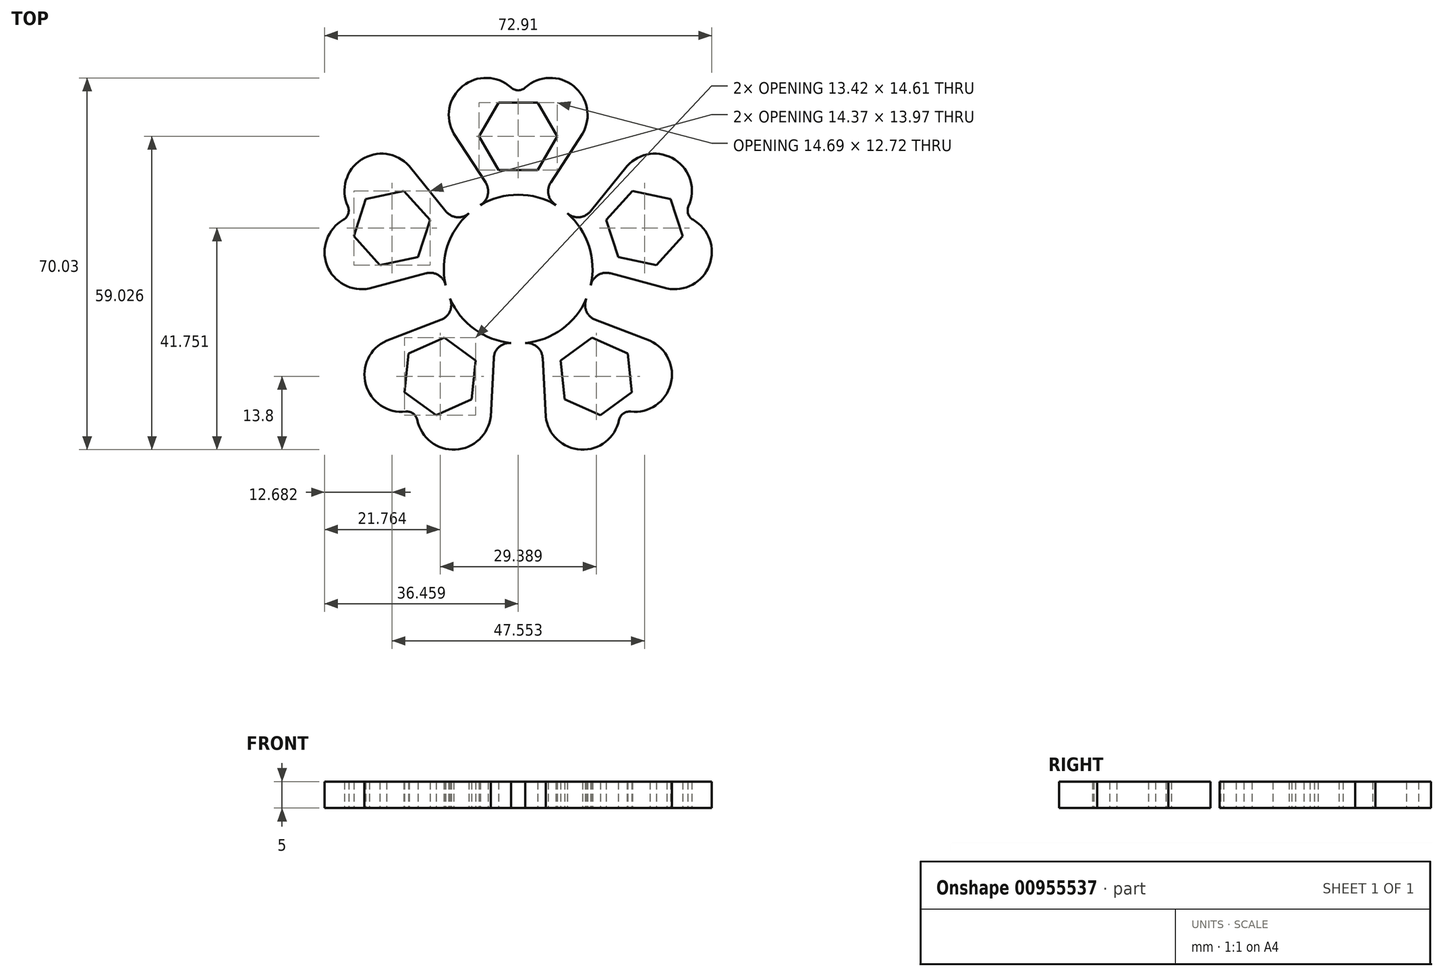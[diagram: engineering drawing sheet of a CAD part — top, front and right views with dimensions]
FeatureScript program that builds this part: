
annotation { "Feature Type Name" : "Feature", "Feature Type Description" : "" }
export const myFeature = defineFeature(function(context is Context, id is Id, definition is map)
    precondition{}
    {
        {
            var Q0;
            Q0=qCreatedBy(makeId("Top.planeOp"),FACE);
            var sketch = newSketch(context, id + "F0", { "sketchPlane" : qUnion([Q0])});
            skLineSegment(sketch, "E0", {"start": v(6.13, 16.29) * mm, "end": v(12.12, 25.52) * mm});
            skArc(sketch, "E1", {"start": v(12.12, 25.52) * mm, "mid": v(10.45, 34.47) * mm, "end": v(1.35, 34.19) * mm});
            skLineSegment(sketch, "E2.trimOffspring", {"start": v(0, 32.52) * mm, "end": v(0, 67.12) * mm, "construction": true});
            skLineSegment(sketch, "E3.trimOffspring", {"start": v(0, 19.02) * mm, "end": v(0, 41.02) * mm, "construction": true});
            skArc(sketch, "E4.MirrorCS", {"start": v(-12.13, 25.52) * mm, "mid": v(-10.45, 34.47) * mm, "end": v(-1.35, 34.19) * mm});
            skPoint(sketch, "E5.visualSharp", {"position": v(0, 32.52) * mm});
            skArc(sketch, "E5.filletArc", {"start": v(-1.35, 34.19) * mm, "mid": v(0, 33.67) * mm, "end": v(1.35, 34.19) * mm});
            skCircle(sketch, "E6.cCircle", {"center": v(0, 25.02) * mm, "radius": 6.36 * mm, "construction": true});
            skLineSegment(sketch, "E6.0", {"start": v(-3.67, 31.38) * mm, "end": v(3.67, 31.38) * mm});
            skLineSegment(sketch, "E6.1", {"start": v(3.67, 31.38) * mm, "end": v(7.34, 25.02) * mm});
            skLineSegment(sketch, "E6.2", {"start": v(7.34, 25.02) * mm, "end": v(3.67, 18.66) * mm});
            skLineSegment(sketch, "E6.3", {"start": v(3.67, 18.66) * mm, "end": v(-3.67, 18.66) * mm});
            skLineSegment(sketch, "E6.4", {"start": v(-3.67, 18.66) * mm, "end": v(-7.35, 25.02) * mm});
            skLineSegment(sketch, "E6.5", {"start": v(-7.35, 25.02) * mm, "end": v(-3.67, 31.38) * mm});
            skPoint(sketch, "E6.0.midPoint", {"position": v(0, 31.38) * mm});
            skCircle(sketch, "E7.0", {"center": v(0, 0.02) * mm, "radius": 14 * mm});
            skArc(sketch, "E8", {"start": v(6.13, 16.29) * mm, "mid": v(5.72, 13.97) * mm, "end": v(7.12, 12.07) * mm});
            skPoint(sketch, "E9.orphan", {"position": v(1.19, 8.67) * mm});
            skPoint(sketch, "E10.orphan", {"position": v(-1.19, 8.67) * mm});
            skArc(sketch, "E11.MirrorCS", {"start": v(-6.13, 16.29) * mm, "mid": v(-5.73, 13.97) * mm, "end": v(-7.12, 12.07) * mm});
            skLineSegment(sketch, "E12", {"start": v(-6.13, 16.29) * mm, "end": v(-12.13, 25.52) * mm});
            skLineSegment(sketch, "E13.1.0", {"start": v(-21.5, 14.73) * mm, "end": v(-16.6, 9.27) * mm});
            skPoint(sketch, "E13.1.1", {"position": v(-30.91, 10.06) * mm});
            skPoint(sketch, "E13.1.2", {"position": v(-29.83, 9.7) * mm});
            skPoint(sketch, "E13.1.3", {"position": v(-7.87, 3.82) * mm});
            skArc(sketch, "E13.1.4", {"start": v(-20.5, 19.43) * mm, "mid": v(-29.54, 20.6) * mm, "end": v(-32.09, 11.86) * mm});
            skCircle(sketch, "E13.1.5", {"center": v(-23.78, 7.74) * mm, "radius": 6.36 * mm, "construction": true});
            skArc(sketch, "E13.1.6", {"start": v(-13.58, 10.87) * mm, "mid": v(-11.5, 9.77) * mm, "end": v(-9.26, 10.51) * mm});
            skLineSegment(sketch, "E13.1.7", {"start": v(-17.37, -0.79) * mm, "end": v(-28, -3.64) * mm});
            skLineSegment(sketch, "E13.1.8", {"start": v(-18.07, 5.89) * mm, "end": v(-39, 12.69) * mm, "construction": true});
            skLineSegment(sketch, "E13.1.9", {"start": v(-18.86, 2.28) * mm, "end": v(-26.05, 0.76) * mm});
            skLineSegment(sketch, "E13.1.10", {"start": v(-28.7, 13.2) * mm, "end": v(-21.5, 14.73) * mm});
            skArc(sketch, "E13.1.11", {"start": v(-28, -3.64) * mm, "mid": v(-36, 0.72) * mm, "end": v(-32.92, 9.3) * mm});
            skLineSegment(sketch, "E13.1.12", {"start": v(-13.58, 10.87) * mm, "end": v(-20.5, 19.43) * mm});
            skLineSegment(sketch, "E13.1.13", {"start": v(-26.05, 0.76) * mm, "end": v(-30.96, 6.21) * mm});
            skPoint(sketch, "E13.1.14", {"position": v(-8.6, 1.56) * mm});
            skLineSegment(sketch, "E13.1.15", {"start": v(-16.6, 9.27) * mm, "end": v(-18.86, 2.28) * mm});
            skArc(sketch, "E13.1.16", {"start": v(-17.37, -0.79) * mm, "mid": v(-15.04, -1.12) * mm, "end": v(-13.67, -3.03) * mm});
            skArc(sketch, "E13.1.17", {"start": v(-32.92, 9.3) * mm, "mid": v(-32, 10.41) * mm, "end": v(-32.09, 11.86) * mm});
            skLineSegment(sketch, "E13.1.18", {"start": v(-30.96, 6.21) * mm, "end": v(-28.7, 13.2) * mm});
            skLineSegment(sketch, "E13.2.0", {"start": v(-20.64, -15.9) * mm, "end": v(-13.93, -12.9) * mm});
            skPoint(sketch, "E13.2.1", {"position": v(-19.1, -26.28) * mm});
            skPoint(sketch, "E13.2.2", {"position": v(-18.43, -25.36) * mm});
            skPoint(sketch, "E13.2.3", {"position": v(-6.05, -6.3) * mm});
            skArc(sketch, "E13.2.4", {"start": v(-24.8, -13.49) * mm, "mid": v(-28.7, -21.71) * mm, "end": v(-21.18, -26.84) * mm});
            skCircle(sketch, "E13.2.5", {"center": v(-14.7, -20.2) * mm, "radius": 6.36 * mm, "construction": true});
            skArc(sketch, "E13.2.6", {"start": v(-14.52, -9.54) * mm, "mid": v(-12.83, -7.9) * mm, "end": v(-12.85, -5.55) * mm});
            skLineSegment(sketch, "E13.2.7", {"start": v(-4.6, -16.75) * mm, "end": v(-5.18, -27.74) * mm});
            skLineSegment(sketch, "E13.2.8", {"start": v(-11.17, -15.36) * mm, "end": v(-24.1, -33.15) * mm, "construction": true});
            skLineSegment(sketch, "E13.2.9", {"start": v(-7.99, -17.22) * mm, "end": v(-8.75, -24.53) * mm});
            skLineSegment(sketch, "E13.2.10", {"start": v(-21.4, -23.2) * mm, "end": v(-20.64, -15.9) * mm});
            skArc(sketch, "E13.2.11", {"start": v(-5.18, -27.74) * mm, "mid": v(-11.8, -34) * mm, "end": v(-19, -28.42) * mm});
            skLineSegment(sketch, "E13.2.12", {"start": v(-14.52, -9.54) * mm, "end": v(-24.8, -13.49) * mm});
            skLineSegment(sketch, "E13.2.13", {"start": v(-8.75, -24.53) * mm, "end": v(-15.46, -27.51) * mm});
            skPoint(sketch, "E13.2.14", {"position": v(-4.13, -7.69) * mm});
            skLineSegment(sketch, "E13.2.15", {"start": v(-13.93, -12.9) * mm, "end": v(-7.99, -17.22) * mm});
            skArc(sketch, "E13.2.16", {"start": v(-4.6, -16.75) * mm, "mid": v(-3.57, -14.64) * mm, "end": v(-1.33, -13.92) * mm});
            skArc(sketch, "E13.2.17", {"start": v(-19, -28.42) * mm, "mid": v(-19.78, -27.2) * mm, "end": v(-21.18, -26.84) * mm});
            skLineSegment(sketch, "E13.2.18", {"start": v(-15.46, -27.51) * mm, "end": v(-21.4, -23.2) * mm});
            skCircle(sketch, "E14", {"center": v(0, 0) * mm, "radius": 9.5 * mm});
            skPoint(sketch, "E15.3.3.0", {"position": v(19.1, -26.28) * mm});
            skPoint(sketch, "E15.4.3.0", {"position": v(18.43, -25.36) * mm});
            skPoint(sketch, "E15.5.3.0", {"position": v(4.13, -7.69) * mm});
            skArc(sketch, "E15.6.3.0", {"start": v(5.18, -27.74) * mm, "mid": v(11.8, -34) * mm, "end": v(19, -28.42) * mm});
            skCircle(sketch, "E15.10.3.0", {"center": v(14.7, -20.2) * mm, "radius": 6.36 * mm, "construction": true});
            skArc(sketch, "E15.12.3.0", {"start": v(4.6, -16.75) * mm, "mid": v(3.57, -14.64) * mm, "end": v(1.32, -13.92) * mm});
            skLineSegment(sketch, "E15.16.3.0", {"start": v(14.52, -9.54) * mm, "end": v(24.8, -13.49) * mm});
            skLineSegment(sketch, "E15.19.3.0", {"start": v(11.17, -15.36) * mm, "end": v(24.1, -33.15) * mm, "construction": true});
            skLineSegment(sketch, "E15.22.3.0", {"start": v(13.93, -12.9) * mm, "end": v(20.63, -15.9) * mm});
            skLineSegment(sketch, "E15.25.3.0", {"start": v(15.46, -27.51) * mm, "end": v(8.75, -24.53) * mm});
            skArc(sketch, "E15.28.3.0", {"start": v(24.8, -13.49) * mm, "mid": v(28.7, -21.71) * mm, "end": v(21.18, -26.84) * mm});
            skLineSegment(sketch, "E15.32.3.0", {"start": v(4.6, -16.75) * mm, "end": v(5.18, -27.74) * mm});
            skLineSegment(sketch, "E15.35.3.0", {"start": v(20.63, -15.9) * mm, "end": v(21.4, -23.2) * mm});
            skPoint(sketch, "E15.38.3.0", {"position": v(6.05, -6.3) * mm});
            skLineSegment(sketch, "E15.39.3.0", {"start": v(7.98, -17.22) * mm, "end": v(13.93, -12.9) * mm});
            skArc(sketch, "E15.42.3.0", {"start": v(14.52, -9.54) * mm, "mid": v(12.83, -7.9) * mm, "end": v(12.84, -5.55) * mm});
            skLineSegment(sketch, "E15.45.3.0", {"start": v(8.75, -24.53) * mm, "end": v(7.98, -17.22) * mm});
            skArc(sketch, "E15.46.3.0", {"start": v(21.18, -26.84) * mm, "mid": v(19.78, -27.2) * mm, "end": v(19, -28.42) * mm});
            skLineSegment(sketch, "E15.50.3.0", {"start": v(21.4, -23.2) * mm, "end": v(15.46, -27.51) * mm});
            skPoint(sketch, "E16.3.4.0", {"position": v(30.9, 10.06) * mm});
            skPoint(sketch, "E16.4.4.0", {"position": v(29.82, 9.7) * mm});
            skPoint(sketch, "E16.5.4.0", {"position": v(8.6, 1.56) * mm});
            skArc(sketch, "E16.6.4.0", {"start": v(28, -3.64) * mm, "mid": v(36, 0.72) * mm, "end": v(32.92, 9.3) * mm});
            skCircle(sketch, "E16.10.4.0", {"center": v(23.78, 7.74) * mm, "radius": 6.36 * mm, "construction": true});
            skArc(sketch, "E16.12.4.0", {"start": v(17.37, -0.79) * mm, "mid": v(15.04, -1.12) * mm, "end": v(13.66, -3.03) * mm});
            skLineSegment(sketch, "E16.16.4.0", {"start": v(13.58, 10.87) * mm, "end": v(20.5, 19.43) * mm});
            skLineSegment(sketch, "E16.19.4.0", {"start": v(18.07, 5.89) * mm, "end": v(39, 12.69) * mm, "construction": true});
            skLineSegment(sketch, "E16.22.4.0", {"start": v(16.6, 9.27) * mm, "end": v(21.5, 14.73) * mm});
            skLineSegment(sketch, "E16.25.4.0", {"start": v(30.96, 6.21) * mm, "end": v(26.04, 0.76) * mm});
            skArc(sketch, "E16.28.4.0", {"start": v(20.5, 19.43) * mm, "mid": v(29.54, 20.6) * mm, "end": v(32.08, 11.86) * mm});
            skLineSegment(sketch, "E16.32.4.0", {"start": v(17.37, -0.79) * mm, "end": v(28, -3.64) * mm});
            skLineSegment(sketch, "E16.35.4.0", {"start": v(21.5, 14.73) * mm, "end": v(28.69, 13.2) * mm});
            skPoint(sketch, "E16.38.4.0", {"position": v(7.87, 3.82) * mm});
            skLineSegment(sketch, "E16.39.4.0", {"start": v(18.86, 2.28) * mm, "end": v(16.6, 9.27) * mm});
            skArc(sketch, "E16.42.4.0", {"start": v(13.58, 10.87) * mm, "mid": v(11.5, 9.77) * mm, "end": v(9.26, 10.51) * mm});
            skLineSegment(sketch, "E16.45.4.0", {"start": v(26.04, 0.76) * mm, "end": v(18.86, 2.28) * mm});
            skArc(sketch, "E16.46.4.0", {"start": v(32.08, 11.86) * mm, "mid": v(32, 10.41) * mm, "end": v(32.92, 9.3) * mm});
            skLineSegment(sketch, "E16.50.4.0", {"start": v(28.69, 13.2) * mm, "end": v(30.96, 6.21) * mm});
            skSolve(sketch);
        }
        {
            var Q0;
            Q0=makeQuery(id+"F0.imprint","IMPRINT",FACE,{"disambiguationData":[TD([[makeQuery(id+"F0.imprint","IMPRINT",EDGE,{"derivedFrom":sQuery(id+"F0.wireOp",EDGE,"E13.1.0")}),1.0]])]});
            var Q1;
            Q1=makeQuery(id+"F0.imprint","IMPRINT",FACE,{"disambiguationData":[TD([[makeQuery(id+"F0.imprint","IMPRINT",EDGE,{"derivedFrom":sQuery(id+"F0.wireOp",EDGE,"E13.2.0")}),1.0]])]});
            var Q2;
            Q2=makeQuery(id+"F0.imprint","IMPRINT",FACE,{"disambiguationData":[TD([[makeQuery(id+"F0.imprint","IMPRINT",EDGE,{"derivedFrom":sQuery(id+"F0.wireOp",EDGE,"E0")}),1.0]])]});
            var Q3;
            Q3=makeQuery(id+"F0.imprint","IMPRINT",FACE,{"disambiguationData":[TD([[makeQuery(id+"F0.imprint","IMPRINT",EDGE,{"derivedFrom":sQuery(id+"F0.wireOp",EDGE,"E15.6.4.0")}),1.0]])]});
            var Q4;
            Q4=makeQuery(id+"F0.imprint","IMPRINT",FACE,{"disambiguationData":[TD([[makeQuery(id+"F0.imprint","IMPRINT",EDGE,{"derivedFrom":sQuery(id+"F0.wireOp",EDGE,"E15.6.3.0")}),1.0]])]});
            var Q5;
            Q5=makeQuery(id+"F0.imprint","IMPRINT",FACE,{"disambiguationData":[TD([[makeQuery(id+"F0.imprint","IMPRINT",EDGE,{"derivedFrom":sQuery(id+"F0.wireOp",EDGE,"E16.6.4.0")}),1.0]])]});
            extrude(context, id + "F1", {"entities" : qUnion([Q0, Q1, Q2, Q3, Q4, Q5]), "depth" : 5 * mm, "offsetDistance" : 25 * mm});
        }
    });
